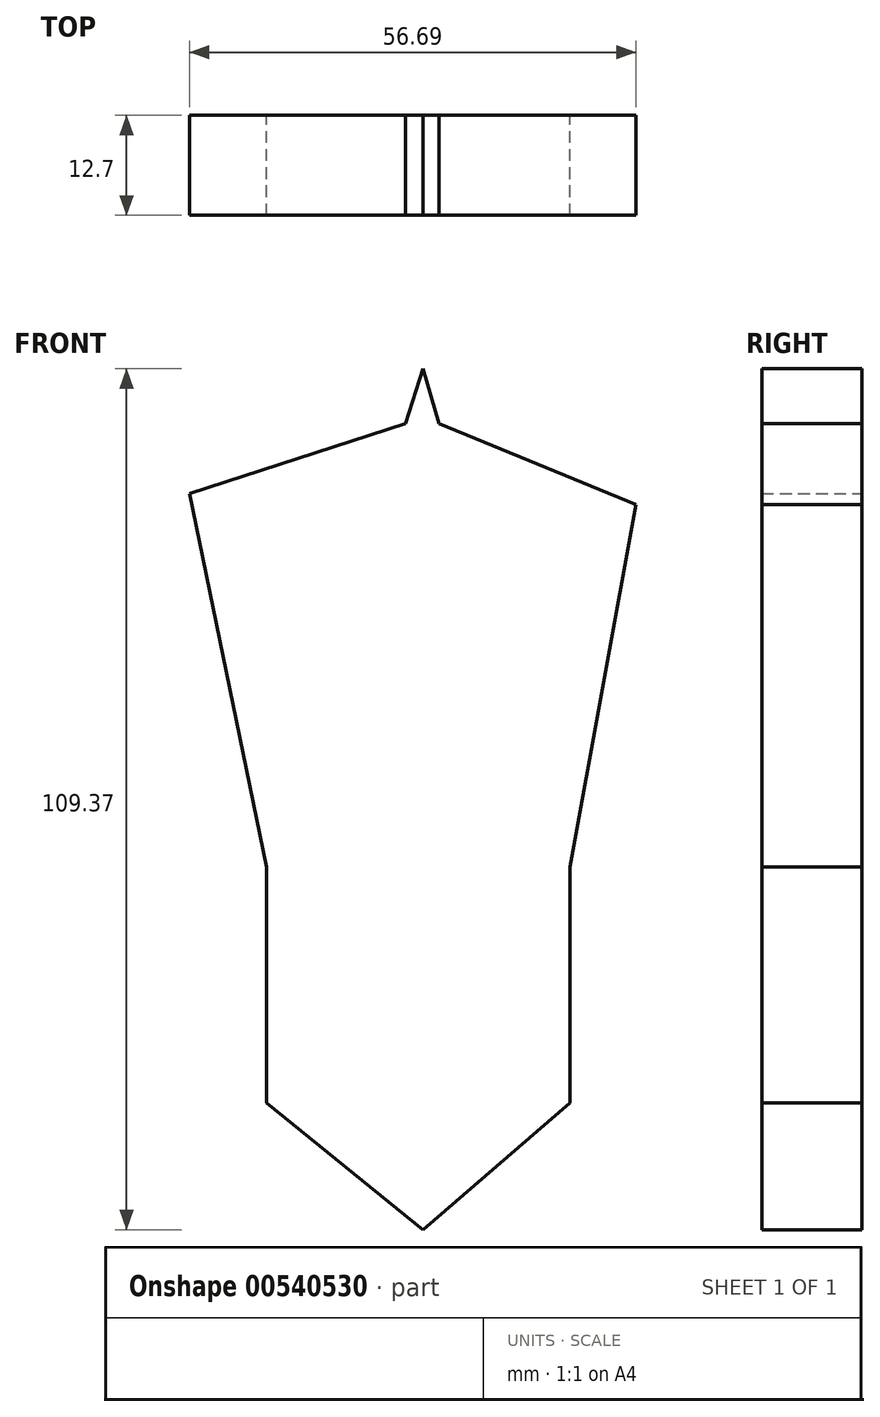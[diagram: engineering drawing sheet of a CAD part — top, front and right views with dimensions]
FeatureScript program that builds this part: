
annotation { "Feature Type Name" : "Feature", "Feature Type Description" : "" }
export const myFeature = defineFeature(function(context is Context, id is Id, definition is map)
    precondition{}
    {
        {
            var Q0;
            Q0=qCreatedBy(makeId("Front.planeOp"),FACE);
            var sketch = newSketch(context, id + "F0", { "sketchPlane" : qUnion([Q0])});
            skLineSegment(sketch, "E0", {"start": v(-19.86, 0) * mm, "end": v(-19.86, -29.93) * mm});
            skLineSegment(sketch, "E1", {"start": v(-19.86, -29.93) * mm, "end": v(0, -46.05) * mm});
            skLineSegment(sketch, "E2", {"start": v(0, -46.05) * mm, "end": v(18.7, -29.93) * mm});
            skLineSegment(sketch, "E3", {"start": v(18.7, -29.93) * mm, "end": v(18.7, 0) * mm});
            skLineSegment(sketch, "E4", {"start": v(18.7, 0) * mm, "end": v(0, 63.32) * mm});
            skLineSegment(sketch, "E5", {"start": v(0, 63.32) * mm, "end": v(-19.86, 0) * mm});
            skLineSegment(sketch, "E6", {"start": v(27.05, 46.05) * mm, "end": v(2.06, 56.34) * mm});
            skLineSegment(sketch, "E7", {"start": v(2.06, 56.34) * mm, "end": v(-2.19, 56.34) * mm});
            skLineSegment(sketch, "E8", {"start": v(-2.19, 56.34) * mm, "end": v(-29.64, 47.49) * mm});
            skLineSegment(sketch, "E9", {"start": v(-29.64, 47.49) * mm, "end": v(-19.86, 0) * mm});
            skLineSegment(sketch, "E10", {"start": v(27.05, 46.05) * mm, "end": v(18.7, 0) * mm});
            skSolve(sketch);
        }
        {
            var Q0;
            Q0 = qSketchRegion(id + "F0", true);
            extrude(context, id + "F1", {"entities" : qUnion([Q0]), "depth" : 12.7 * mm, "offsetDistance" : 25.4 * mm});
        }
    });
